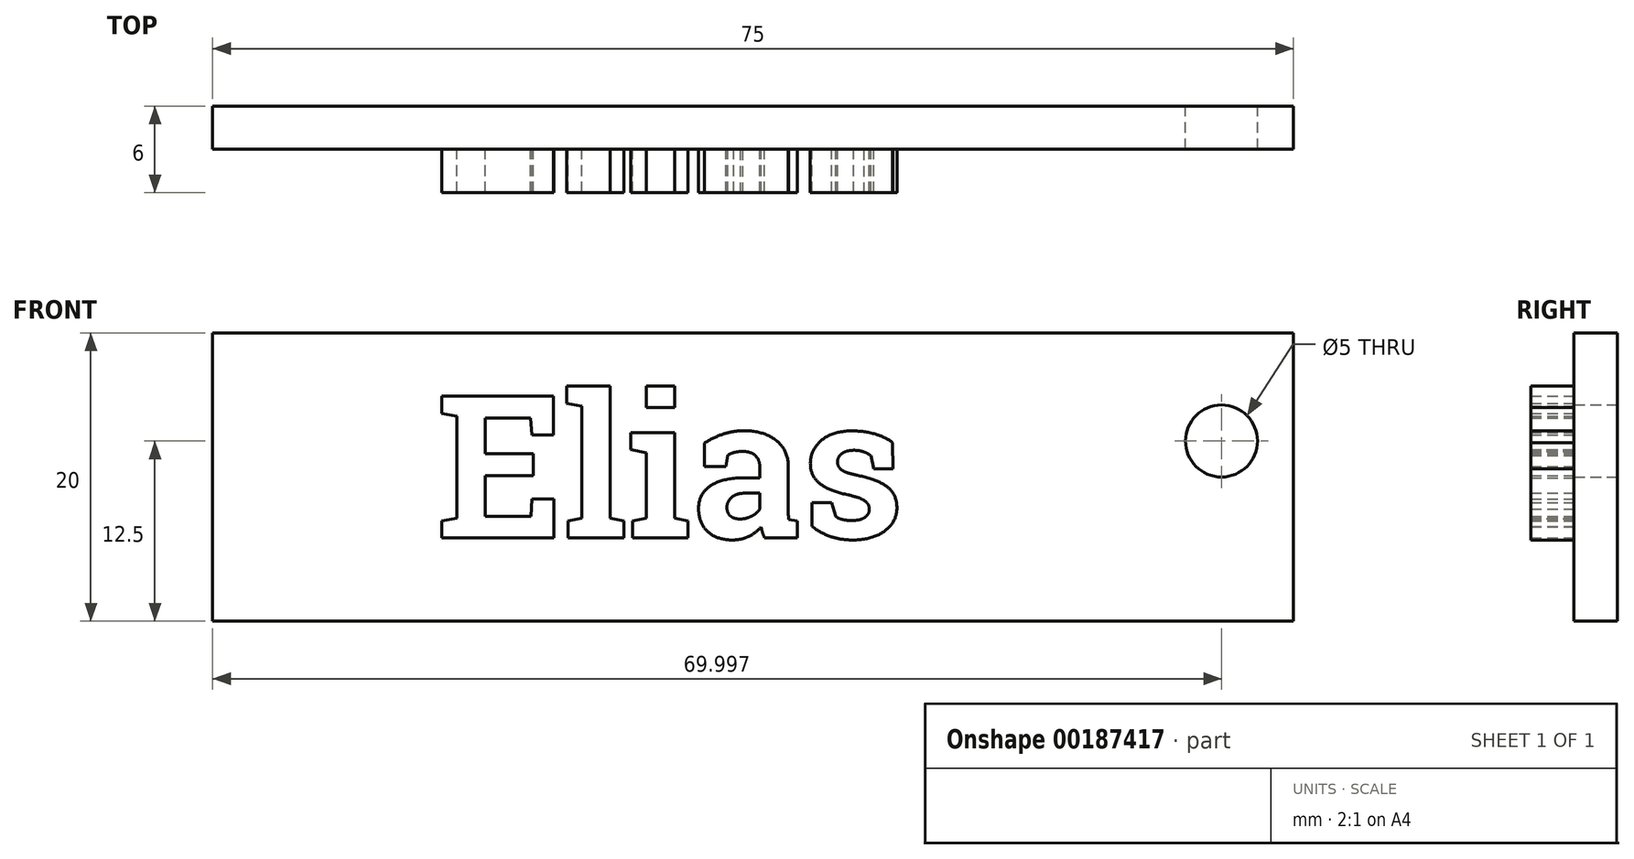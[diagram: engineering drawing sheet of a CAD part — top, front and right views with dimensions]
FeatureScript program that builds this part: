
annotation { "Feature Type Name" : "Feature", "Feature Type Description" : "" }
export const myFeature = defineFeature(function(context is Context, id is Id, definition is map)
    precondition{}
    {
        {
            var Q0;
            Q0=qCreatedBy(makeId("Front.planeOp"),FACE);
            var sketch = newSketch(context, id + "F0", { "sketchPlane" : qUnion([Q0])});
            skLineSegment(sketch, "E0.bottom", {"start": v(-0.08, -0.3) * mm, "end": v(74.92, -0.3) * mm});
            skLineSegment(sketch, "E0.top", {"start": v(-0.08, -20.3) * mm, "end": v(74.92, -20.3) * mm});
            skLineSegment(sketch, "E0.left", {"start": v(-0.08, -0.3) * mm, "end": v(-0.08, -20.3) * mm});
            skLineSegment(sketch, "E0.right", {"start": v(74.92, -0.3) * mm, "end": v(74.92, -20.3) * mm});
            skCircle(sketch, "E1", {"center": v(69.92, -7.8) * mm, "radius": 2.5 * mm});
            skSolve(sketch);
        }
        {
            var Q0;
            Q0 = qSketchRegion(id + "F0", true);
            extrude(context, id + "F1", {"entities" : qUnion([Q0]), "depth" : 3 * mm});
        }
        {
            var Q0;
            Q0=makeQuery(id+"F1.opExtrude","CAP_FACE",FACE,{"disambiguationData":[OSD([sQuery(id+"F0.wireOp",EDGE,"E0.bottom"),sQuery(id+"F0.wireOp",EDGE,"E0.top"),sQuery(id+"F0.wireOp",EDGE,"E0.left"),sQuery(id+"F0.wireOp",EDGE,"E0.right"),sQuery(id+"F0.wireOp",EDGE,"E1")])],"isStart":false});
            var sketch = newSketch(context, id + "F2", { "sketchPlane" : qUnion([Q0])});
            skText(sketch, "E2", { "text": "Elias", "fontName": "RobotoSlab-Bold.ttf"});
            const initialGuessF2  = {"E2": [0.01543, -0.01454, 1, 0, 0.00996]};
            skSetInitialGuess(sketch, initialGuessF2);
            skSolve(sketch);
        }
        {
            var Q0;
            Q0 = qSketchRegion(id + "F2", true);
            extrude(context, id + "F3", {"entities" : qUnion([Q0]), "operationType" : NewBodyOperationType.ADD, "depth" : 3 * mm});
        }
    });
